# Revit family: Door_Sliding_Dunbarton_2-Panel-Marker
name_source: partatom
category: Doors
units: mm (PartAtom-declared; Revit-internal decimal feet)

## family parameters
Always vertical = Yes
Classification Number = 23.30.10.17.17
Cut with Voids When Loaded = No
Host = Wall
Room Calculation Point = No
Shared = No

## types (3) — shared parameters
Air Infiltration = as Specified
Assembly Code = C1020100
Description = Dunbarton Sliding Marker Door - Model Marker as Specified
Door Panel Type = as Specified
Door Thickness = 0' - 1 1/4"
Fire Rating = as Specified
Frame Thickness = 0' - 0 5/8"
Function = Interior
Green Building-LEED = http://www.arcat.com
Impact Resistance = as Specified
Installation-Fabrication = https://dunbarton.com
Keynote = 08 11 10
Manufacturer = Dunbarton Corporation
Manufacturer Fax = 334-793-7022
Manufacturer Website = https://dunbarton.com
Model = Model Marker
Opening Height = 6' - 8"
Product Data = http://www.arcat.com
Product Properties = https://dunbarton.com
RO Spacing Sides = 0' - 0"
RO Spacing Top = 0' - 0"
Rough Height = 0' - 0"
Rough Width = 0' - 0"
Sales Information = https://dunbarton.com
Specification = http://www.arcat.com
Structural Test Pressure = as Specified
Thickness = 0' - 0"
Track A = No
Track B = No
Track C = Yes
URL = https://dunbarton.com
Wall Closure = By host
Water Penetration = as Specified
zero-valued in all types: Expected Lifespan (Years), Maintenance Schedule (Months), R-Value, Warranty Duration (Years)

## per-type parameters (varying)
| type | Unit Width | Width |
| 72 W x 80 H | 5' - 11 1/2" | 5' - 11 1/2" |
| 60 W x 80 H | 4' - 11 1/2" | 4' - 11 1/2" |
| 48 W x 80 H | 3' - 11 1/2" | 3' - 11 1/2" |

## geometry (parser evidence)
native form markers: Blend x4, Sweep x5
no freeform markers — native parametric forms only
